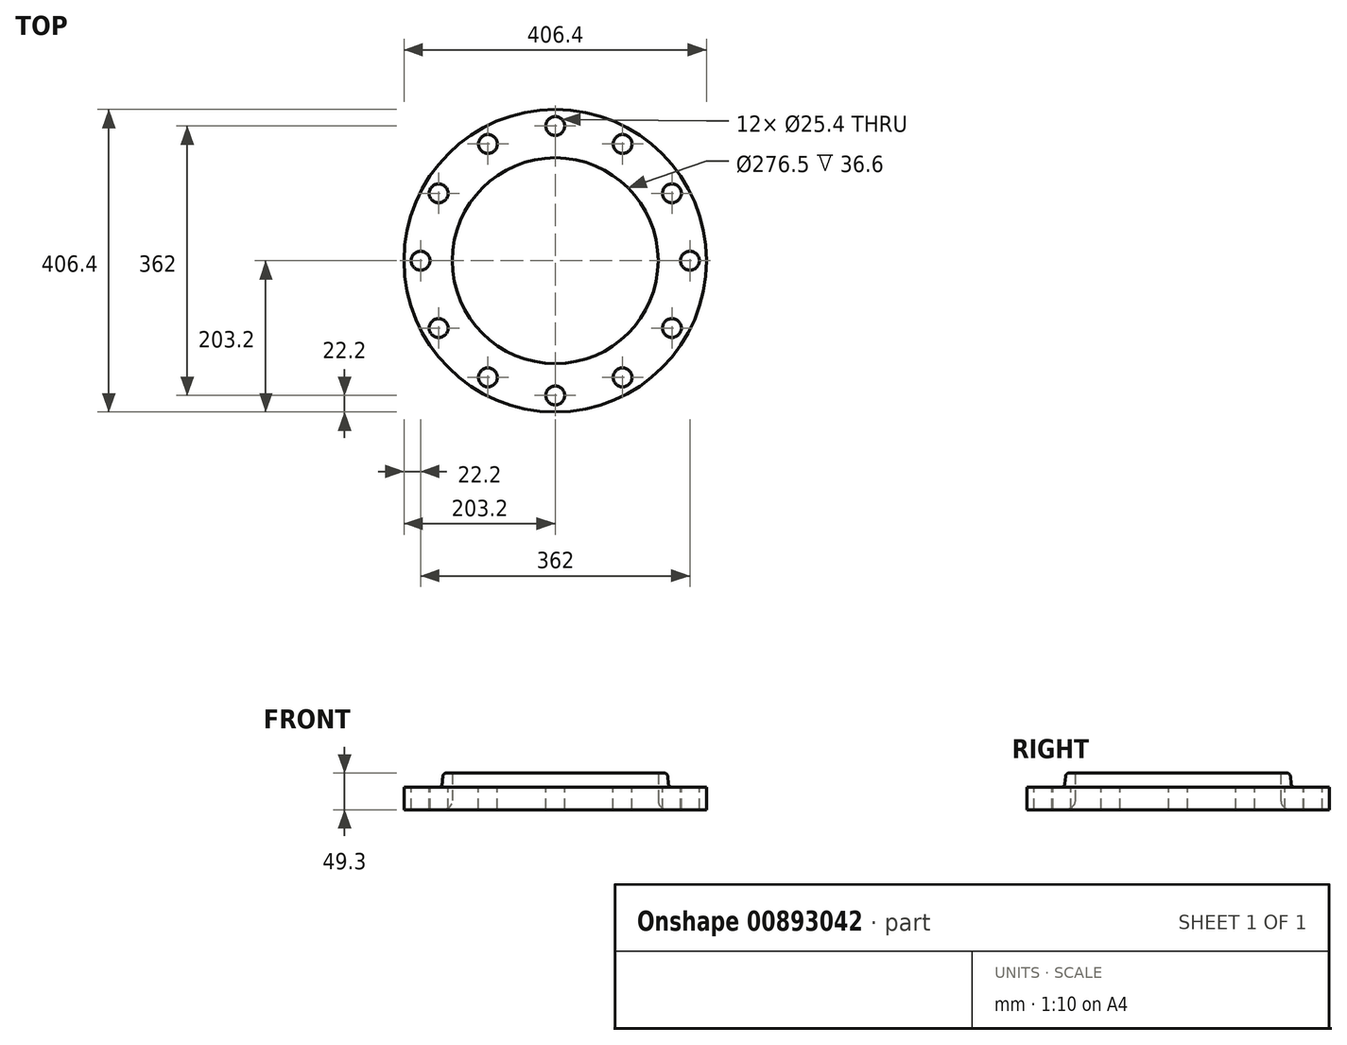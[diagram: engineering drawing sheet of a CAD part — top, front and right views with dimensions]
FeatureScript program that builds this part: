
annotation { "Feature Type Name" : "Feature", "Feature Type Description" : "" }
export const myFeature = defineFeature(function(context is Context, id is Id, definition is map)
    precondition{}
    {
        {
            var Q0;
            Q0=qCreatedBy(makeId("Front.planeOp"),FACE);
            var sketch = newSketch(context, id + "F0", { "sketchPlane" : qUnion([Q0])});
            skLineSegment(sketch, "E0", {"start": v(150.95, 0) * mm, "end": v(203.2, 0) * mm});
            skLineSegment(sketch, "E1", {"start": v(203.2, 0) * mm, "end": v(203.2, 30.2) * mm});
            skLineSegment(sketch, "E2", {"start": v(203.2, 30.2) * mm, "end": v(156.98, 30.2) * mm});
            skLineSegment(sketch, "E3", {"start": v(152, 34.76) * mm, "end": v(151.13, 44.74) * mm});
            skLineSegment(sketch, "E4", {"start": v(146.15, 49.3) * mm, "end": v(138.25, 49.3) * mm});
            skLineSegment(sketch, "E5", {"start": v(138.25, 49.3) * mm, "end": v(138.25, 12.7) * mm});
            skLineSegment(sketch, "E6", {"start": v(0, 0) * mm, "end": v(0, 49.3) * mm});
            skPoint(sketch, "E7.visualSharp", {"position": v(138.25, 0) * mm});
            skArc(sketch, "E7.filletArc", {"start": v(138.25, 12.7) * mm, "mid": v(141.97, 3.72) * mm, "end": v(150.95, 0) * mm});
            skPoint(sketch, "E8.visualSharp", {"position": v(150.73, 49.3) * mm});
            skArc(sketch, "E8.filletArc", {"start": v(151.13, 44.74) * mm, "mid": v(149.53, 47.99) * mm, "end": v(146.15, 49.3) * mm});
            skPoint(sketch, "E9.visualSharp", {"position": v(152.4, 30.2) * mm});
            skArc(sketch, "E9.filletArc", {"start": v(152, 34.76) * mm, "mid": v(153.6, 31.51) * mm, "end": v(156.98, 30.2) * mm});
            skSolve(sketch);
        }
        {
            var Q0;
            Q0=makeQuery(id+"F0.imprint","IMPRINT",FACE,{"disambiguationData":[TD([[makeQuery(id+"F0.imprint","IMPRINT",EDGE,{"derivedFrom":sQuery(id+"F0.wireOp",EDGE,"E0")}),1.0]])]});
            var Q1;
            Q1=sQuery(id+"F0.wireOp",EDGE,"E6");
            revolve(context, id + "F1", {"entities" : qUnion([Q0]), "axis" : qUnion([Q1]), "revolveType" : RevolveType.FULL});
        }
        {
            var Q0;
            Q0=makeQuery(id+"F1.opRevolve","SWEPT_FACE",FACE,{"disambiguationData":[OSD([sQuery(id+"F0.wireOp",EDGE,"E2")])]});
            var sketch = newSketch(context, id + "F2", { "sketchPlane" : qUnion([Q0])});
            skCircle(sketch, "E10", {"center": v(0, 0) * mm, "radius": 181 * mm, "construction": true});
            skCircle(sketch, "E11", {"center": v(0, 181) * mm, "radius": 12.7 * mm});
            skCircle(sketch, "E12.1.0", {"center": v(-90.5, 156.75) * mm, "radius": 12.7 * mm});
            skCircle(sketch, "E12.2.0", {"center": v(-156.75, 90.5) * mm, "radius": 12.7 * mm});
            skCircle(sketch, "E12.3.0", {"center": v(-181, 0) * mm, "radius": 12.7 * mm});
            skCircle(sketch, "E12.4.0", {"center": v(-156.75, -90.5) * mm, "radius": 12.7 * mm});
            skCircle(sketch, "E12.5.0", {"center": v(-90.5, -156.75) * mm, "radius": 12.7 * mm});
            skCircle(sketch, "E12.6.0", {"center": v(0, -181) * mm, "radius": 12.7 * mm});
            skCircle(sketch, "E12.7.0", {"center": v(90.5, -156.75) * mm, "radius": 12.7 * mm});
            skCircle(sketch, "E12.8.0", {"center": v(156.75, -90.5) * mm, "radius": 12.7 * mm});
            skCircle(sketch, "E12.9.0", {"center": v(181, 0) * mm, "radius": 12.7 * mm});
            skCircle(sketch, "E12.10.0", {"center": v(156.75, 90.5) * mm, "radius": 12.7 * mm});
            skCircle(sketch, "E12.11.0", {"center": v(90.5, 156.75) * mm, "radius": 12.7 * mm});
            skSolve(sketch);
        }
        {
            var Q0;
            Q0=qSketchRegion(id+"F2",true);
            extrude(context, id + "F3", {"entities" : qUnion([Q0]), "operationType" : NewBodyOperationType.REMOVE, "endBound" : BoundingType.THROUGH_ALL, "oppositeDirection" : true, "depth" : 25 * mm, "offsetDistance" : 25 * mm});
        }
    });
